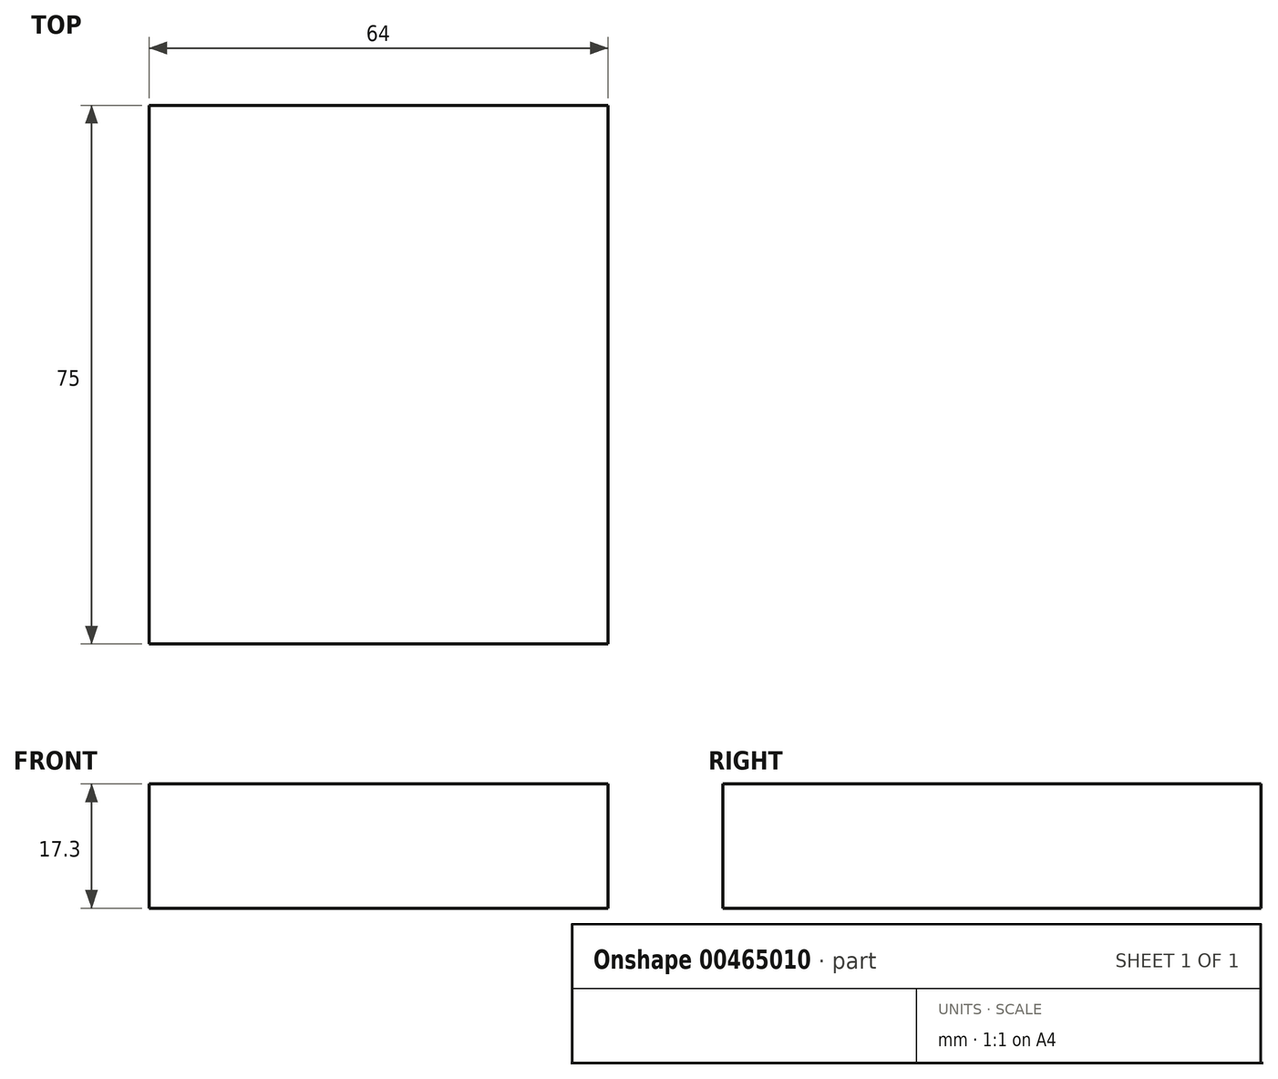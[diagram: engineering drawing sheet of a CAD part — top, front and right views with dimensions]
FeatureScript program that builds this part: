
annotation { "Feature Type Name" : "Feature", "Feature Type Description" : "" }
export const myFeature = defineFeature(function(context is Context, id is Id, definition is map)
    precondition{}
    {
        {
            var Q0;
            Q0=qCreatedBy(makeId("Top.planeOp"),FACE);
            var sketch = newSketch(context, id + "F0", { "sketchPlane" : qUnion([Q0])});
            skLineSegment(sketch, "E0.bottom", {"start": v(0, 0) * mm, "end": v(64, 0) * mm});
            skLineSegment(sketch, "E0.top", {"start": v(0, 75) * mm, "end": v(64, 75) * mm});
            skLineSegment(sketch, "E0.left", {"start": v(0, 0) * mm, "end": v(0, 75) * mm});
            skLineSegment(sketch, "E0.right", {"start": v(64, 0) * mm, "end": v(64, 75) * mm});
            skSolve(sketch);
        }
        {
            var Q0;
            Q0=makeQuery(id+"F0.imprint","IMPRINT",FACE,{"disambiguationData":[TD([[makeQuery(id+"F0.imprint","IMPRINT",EDGE,{"derivedFrom":sQuery(id+"F0.wireOp",EDGE,"E0.bottom")}),1.0]])]});
            extrude(context, id + "F1", {"entities" : qUnion([Q0]), "depth" : 17.3 * mm});
        }
    });
